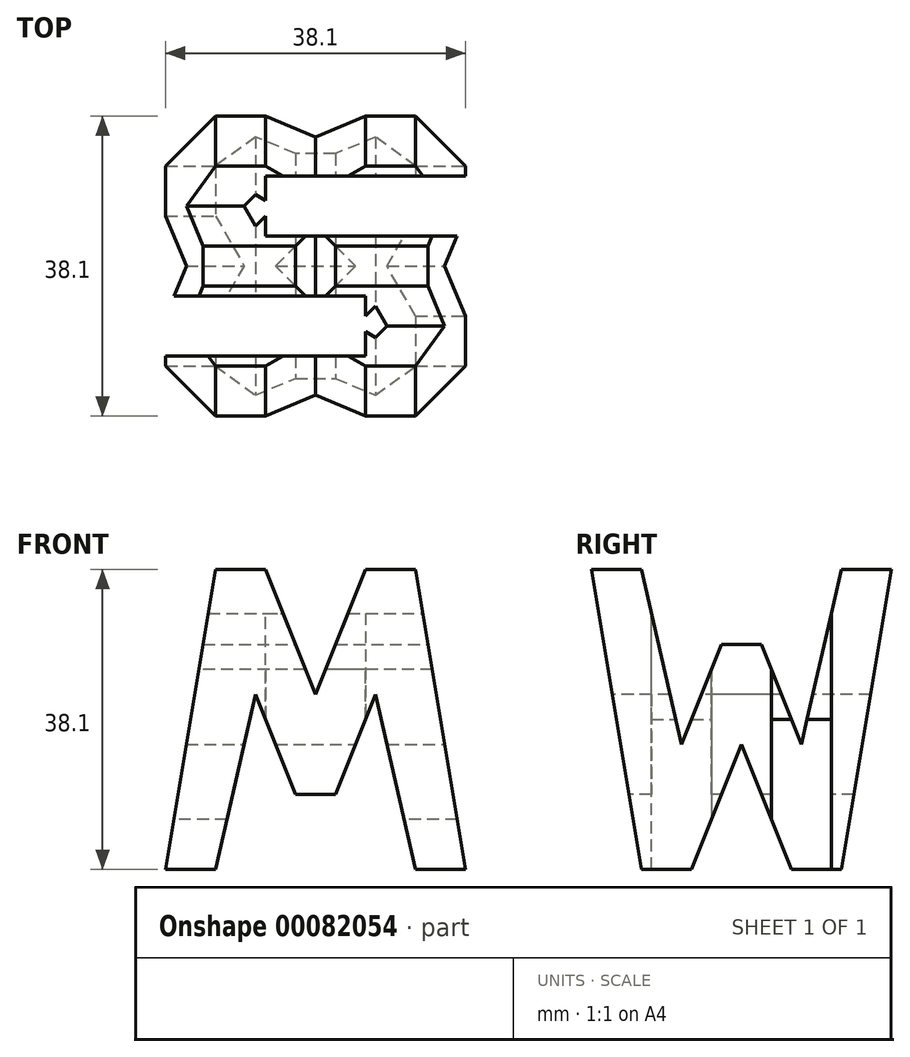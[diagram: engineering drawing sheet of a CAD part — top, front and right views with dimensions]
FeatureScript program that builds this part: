
annotation { "Feature Type Name" : "Feature", "Feature Type Description" : "" }
export const myFeature = defineFeature(function(context is Context, id is Id, definition is map)
    precondition{}
    {
        {
            var Q0;
            Q0=qCreatedBy(makeId("Front.planeOp"),FACE);
            var sketch = newSketch(context, id + "F0", { "sketchPlane" : qUnion([Q0])});
            skLineSegment(sketch, "E0", {"start": v(0, 0) * mm, "end": v(0, 38.1) * mm});
            skLineSegment(sketch, "E1", {"start": v(0, 38.1) * mm, "end": v(38.1, 38.1) * mm});
            skLineSegment(sketch, "E2", {"start": v(38.1, 38.1) * mm, "end": v(38.1, 0) * mm});
            skLineSegment(sketch, "E3", {"start": v(38.1, 0) * mm, "end": v(0, 0) * mm});
            skSolve(sketch);
        }
        {
            var Q0;
            Q0 = qSketchRegion(id + "F0", true);
            extrude(context, id + "F1", {"entities" : qUnion([Q0]), "depth" : 38.1 * mm});
        }
        {
            var Q0;
            Q0=qCreatedBy(makeId("Front.planeOp"),FACE);
            cPlane(context, id + "F2", {"entities" : qUnion([Q0]), "cplaneType" : CPlaneType.OFFSET, "offset" : 38.1 * mm, "width" : 152.4 * mm, "height" : 152.4 * mm});
        }
        {
            var Q0;
            Q0=qCreatedBy(makeId("Right.planeOp"),FACE);
            cPlane(context, id + "F3", {"entities" : qUnion([Q0]), "cplaneType" : CPlaneType.OFFSET, "offset" : 38.1 * mm, "width" : 152.4 * mm, "height" : 152.4 * mm});
        }
        {
            var Q0;
            Q0=qCreatedBy(makeId("Top.planeOp"),FACE);
            cPlane(context, id + "F4", {"entities" : qUnion([Q0]), "cplaneType" : CPlaneType.OFFSET, "offset" : 38.1 * mm, "width" : 152.4 * mm, "height" : 152.4 * mm});
        }
        {
            var Q0;
            Q0=qCreatedBy(id+"F3.planeOp",FACE);
            var sketch = newSketch(context, id + "F5", { "sketchPlane" : qUnion([Q0])});
            skLineSegment(sketch, "E4", {"start": v(0, 0) * mm, "end": v(0, 38.1) * mm});
            skLineSegment(sketch, "E5", {"start": v(0, 38.1) * mm, "end": v(-38.1, 38.1) * mm});
            skLineSegment(sketch, "E6", {"start": v(-38.1, 38.1) * mm, "end": v(-38.1, 0) * mm});
            skLineSegment(sketch, "E7", {"start": v(-38.1, 0) * mm, "end": v(0, 0) * mm});
            skLineSegment(sketch, "E8", {"start": v(-38.1, 38.1) * mm, "end": v(-31.75, 0) * mm});
            skLineSegment(sketch, "E9", {"start": v(-31.75, 38.1) * mm, "end": v(-26.67, 15.87) * mm});
            skLineSegment(sketch, "E10", {"start": v(-26.67, 15.88) * mm, "end": v(-21.59, 28.57) * mm});
            skLineSegment(sketch, "E11", {"start": v(-21.59, 28.57) * mm, "end": v(-16.5, 28.57) * mm});
            skLineSegment(sketch, "E12", {"start": v(-16.5, 28.57) * mm, "end": v(-11.43, 15.88) * mm});
            skLineSegment(sketch, "E13", {"start": v(-25.4, 0) * mm, "end": v(-19.05, 15.87) * mm});
            skLineSegment(sketch, "E14", {"start": v(-6.35, 0) * mm, "end": v(0, 38.1) * mm});
            skLineSegment(sketch, "E15", {"start": v(-11.43, 15.88) * mm, "end": v(-6.35, 38.1) * mm});
            skLineSegment(sketch, "E16", {"start": v(-19.05, 15.88) * mm, "end": v(-12.7, 0) * mm});
            skSolve(sketch);
        }
        {
            var Q0;
            {var subQ0=sQuery(id+"F5.wireOp",EDGE,"E13");Q0=makeQuery(id+"F5.imprint","IMPRINT",FACE,{"disambiguationData":[TD([[makeQuery(id+"F5.imprint","IMPRINT",EDGE,{"derivedFrom":subQ0}),-1.0]])]});}
            var Q1;
            {var subQ0=sQuery(id+"F5.wireOp",EDGE,"E9");Q1=makeQuery(id+"F5.imprint","IMPRINT",FACE,{"disambiguationData":[TD([[makeQuery(id+"F5.imprint","IMPRINT",EDGE,{"derivedFrom":subQ0}),1.0]])]});}
            var Q2;
            {var subQ0=sQuery(id+"F5.wireOp",EDGE,"E6");Q2=makeQuery(id+"F5.imprint","IMPRINT",FACE,{"disambiguationData":[TD([[makeQuery(id+"F5.imprint","IMPRINT",EDGE,{"derivedFrom":subQ0}),1.0]])]});}
            var Q3;
            {var subQ0=sQuery(id+"F5.wireOp",EDGE,"E4");Q3=makeQuery(id+"F5.imprint","IMPRINT",FACE,{"disambiguationData":[TD([[makeQuery(id+"F5.imprint","IMPRINT",EDGE,{"derivedFrom":subQ0}),1.0]])]});}
            extrude(context, id + "F6", {"entities" : qUnion([Q0, Q1, Q2, Q3]), "operationType" : NewBodyOperationType.REMOVE, "oppositeDirection" : true, "depth" : 38.1 * mm});
        }
        {
            var Q0;
            Q0=qCreatedBy(id+"F2.planeOp",FACE);
            var sketch = newSketch(context, id + "F7", { "sketchPlane" : qUnion([Q0])});
            skLineSegment(sketch, "E17", {"start": v(0, 0) * mm, "end": v(0, 38.1) * mm});
            skLineSegment(sketch, "E18", {"start": v(0, 38.1) * mm, "end": v(38.1, 38.1) * mm});
            skLineSegment(sketch, "E19", {"start": v(38.1, 38.1) * mm, "end": v(38.1, 0) * mm});
            skLineSegment(sketch, "E20", {"start": v(38.1, 0) * mm, "end": v(0, 0) * mm});
            skLineSegment(sketch, "E21", {"start": v(0, 0) * mm, "end": v(6.35, 38.1) * mm});
            skLineSegment(sketch, "E22", {"start": v(12.7, 38.1) * mm, "end": v(19.05, 22.22) * mm});
            skLineSegment(sketch, "E23", {"start": v(31.75, 38.1) * mm, "end": v(38.1, 0) * mm});
            skLineSegment(sketch, "E24", {"start": v(19.05, 22.22) * mm, "end": v(25.4, 38.1) * mm});
            skLineSegment(sketch, "E25", {"start": v(6.35, 0) * mm, "end": v(11.43, 22.23) * mm});
            skLineSegment(sketch, "E26", {"start": v(11.43, 22.23) * mm, "end": v(16.51, 9.53) * mm});
            skLineSegment(sketch, "E27", {"start": v(16.51, 9.53) * mm, "end": v(21.6, 9.53) * mm});
            skLineSegment(sketch, "E28", {"start": v(21.59, 9.53) * mm, "end": v(26.67, 22.22) * mm});
            skLineSegment(sketch, "E29", {"start": v(26.67, 22.22) * mm, "end": v(31.75, 0) * mm});
            skSolve(sketch);
        }
        {
            var Q0;
            {var subQ0=sQuery(id+"F7.wireOp",EDGE,"E25");Q0=makeQuery(id+"F7.imprint","IMPRINT",FACE,{"disambiguationData":[TD([[makeQuery(id+"F7.imprint","IMPRINT",EDGE,{"derivedFrom":subQ0}),-1.0]])]});}
            var Q1;
            {var subQ0=sQuery(id+"F7.wireOp",EDGE,"E22");Q1=makeQuery(id+"F7.imprint","IMPRINT",FACE,{"disambiguationData":[TD([[makeQuery(id+"F7.imprint","IMPRINT",EDGE,{"derivedFrom":subQ0}),1.0]])]});}
            var Q2;
            {var subQ0=sQuery(id+"F7.wireOp",EDGE,"E17");Q2=makeQuery(id+"F7.imprint","IMPRINT",FACE,{"disambiguationData":[TD([[makeQuery(id+"F7.imprint","IMPRINT",EDGE,{"derivedFrom":subQ0}),-1.0]])]});}
            var Q3;
            {var subQ0=sQuery(id+"F7.wireOp",EDGE,"E19");Q3=makeQuery(id+"F7.imprint","IMPRINT",FACE,{"disambiguationData":[TD([[makeQuery(id+"F7.imprint","IMPRINT",EDGE,{"derivedFrom":subQ0}),-1.0]])]});}
            extrude(context, id + "F8", {"entities" : qUnion([Q0, Q1, Q2, Q3]), "operationType" : NewBodyOperationType.REMOVE, "oppositeDirection" : true, "depth" : 38.1 * mm});
        }
        {
            var Q0;
            Q0=qCreatedBy(id+"F4.planeOp",FACE);
            var sketch = newSketch(context, id + "F9", { "sketchPlane" : qUnion([Q0])});
            skLineSegment(sketch, "E30", {"start": v(0, 0) * mm, "end": v(38.1, 0) * mm});
            skLineSegment(sketch, "E31", {"start": v(38.1, 0) * mm, "end": v(38.1, -38.1) * mm});
            skLineSegment(sketch, "E32", {"start": v(38.1, -38.1) * mm, "end": v(0, -38.1) * mm});
            skLineSegment(sketch, "E33", {"start": v(0, -38.1) * mm, "end": v(0, 0) * mm});
            skLineSegment(sketch, "E34", {"start": v(38.1, -7.62) * mm, "end": v(12.7, -7.62) * mm});
            skLineSegment(sketch, "E35", {"start": v(12.7, -7.62) * mm, "end": v(12.7, -15.24) * mm});
            skLineSegment(sketch, "E36", {"start": v(12.7, -15.24) * mm, "end": v(38.1, -15.24) * mm});
            skLineSegment(sketch, "E37", {"start": v(0, -22.86) * mm, "end": v(25.4, -22.86) * mm});
            skLineSegment(sketch, "E38", {"start": v(25.4, -22.86) * mm, "end": v(25.4, -30.48) * mm});
            skLineSegment(sketch, "E39", {"start": v(25.4, -30.48) * mm, "end": v(0, -30.48) * mm});
            skSolve(sketch);
        }
        {
            var Q0;
            {var subQ0=sQuery(id+"F9.wireOp",EDGE,"E34");Q0=makeQuery(id+"F9.imprint","IMPRINT",FACE,{"disambiguationData":[TD([[makeQuery(id+"F9.imprint","IMPRINT",EDGE,{"derivedFrom":subQ0}),1.0]])]});}
            var Q1;
            {var subQ0=sQuery(id+"F9.wireOp",EDGE,"E37");Q1=makeQuery(id+"F9.imprint","IMPRINT",FACE,{"disambiguationData":[TD([[makeQuery(id+"F9.imprint","IMPRINT",EDGE,{"derivedFrom":subQ0}),-1.0]])]});}
            extrude(context, id + "F10", {"entities" : qUnion([Q0, Q1]), "operationType" : NewBodyOperationType.REMOVE, "oppositeDirection" : true, "depth" : 38.1 * mm});
        }
    });
